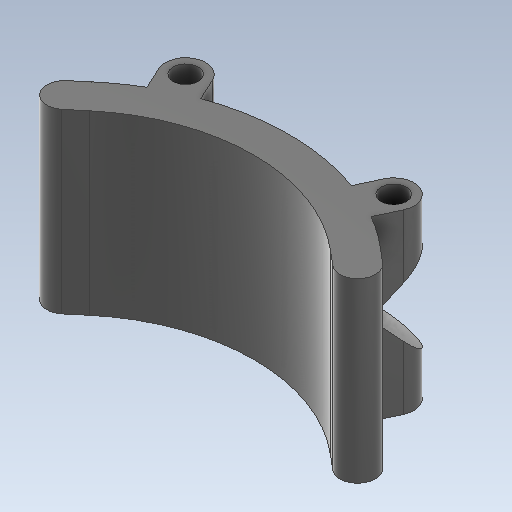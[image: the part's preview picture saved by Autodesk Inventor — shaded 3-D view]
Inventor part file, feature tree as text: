
AUTODESK INVENTOR PART (.ipt)
format: ipt  version: 2020 (Build 240168000, 168)  size: 429,056 bytes
history: native  units: mm
features: sketch x5, extrude x4, projected_geometry x2, other x1, sweep x1
ambient origin geometry x8: Origin, YZ Plane, XZ Plane, XY Plane, X Axis, Y Axis, Z Axis, Center Point
bodies: Body1 (feature_tree)
feature tree (13):
  other  "Твердое тело1"
  extrude  "Выдавливание1"  Depth=35.0mm TaperAngle=0.0deg
  sketch  "Эскиз2"
  extrude  "Выдавливание2"  Depth=4.0mm
  sweep  "Сдвиг1"
  extrude  "Выдавливание5"  Depth=8.0mm
  extrude  "Выдавливание6"  Depth=35.0mm TaperAngle=0.0deg
  sketch  "Эскиз1"
  sketch  "Эскиз3"
  projected_geometry  "Спроецированная петля1"
  projected_geometry  "Спроецированная петля2"
  sketch  "3D эскиз1"
  sketch  "Эскиз4"
